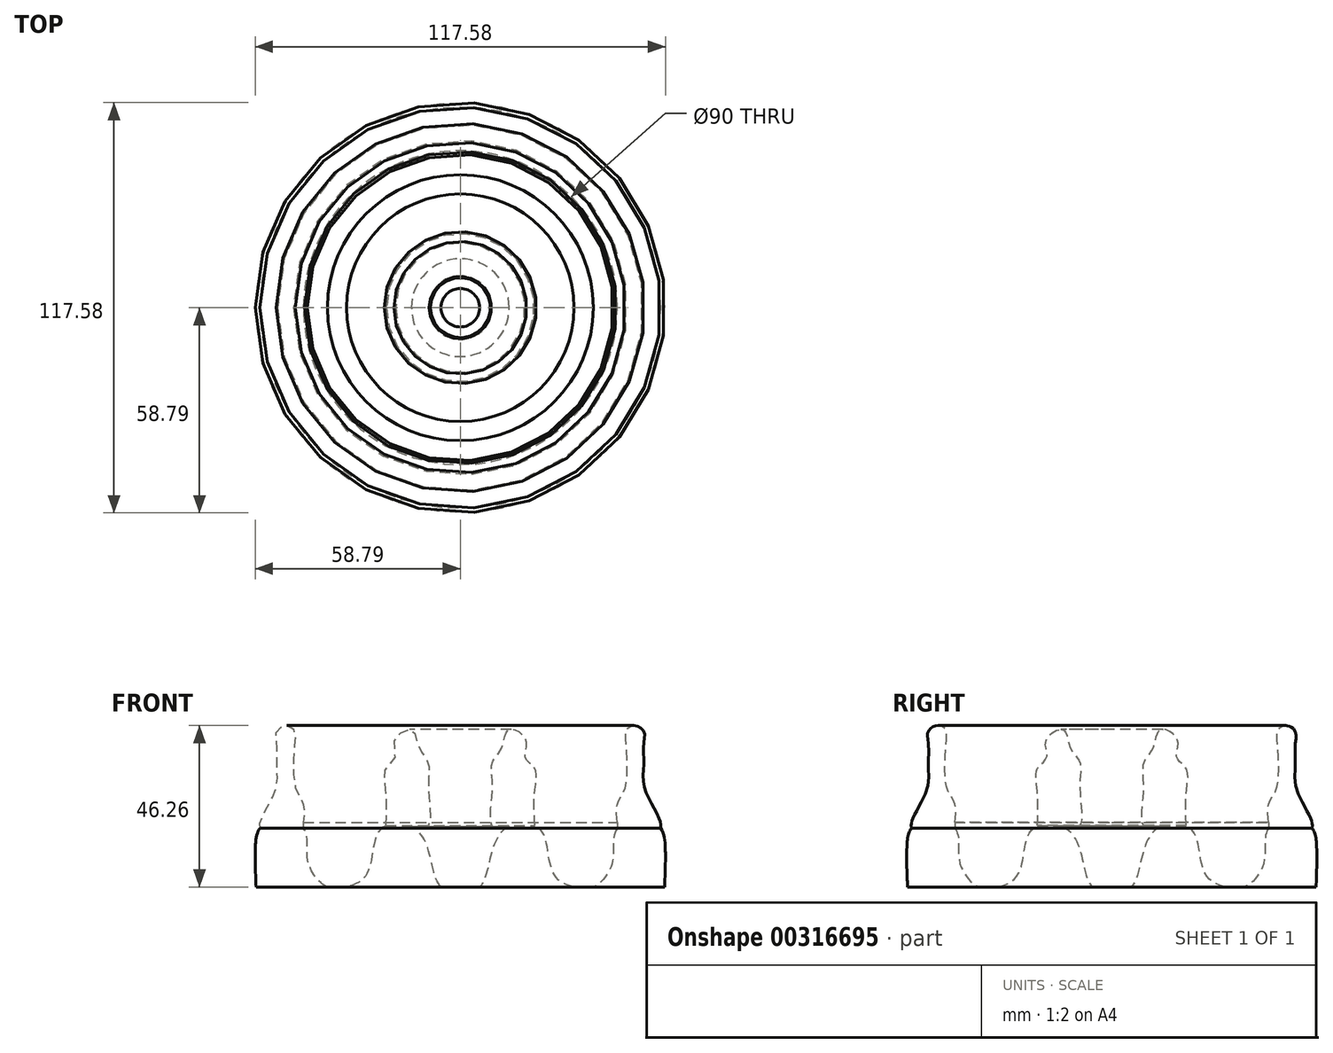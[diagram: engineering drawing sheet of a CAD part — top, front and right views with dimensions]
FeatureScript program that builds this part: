
annotation { "Feature Type Name" : "Feature", "Feature Type Description" : "" }
export const myFeature = defineFeature(function(context is Context, id is Id, definition is map)
    precondition{}
    {
        {
            var Q0;
            Q0=qCreatedBy(makeId("Front.planeOp"),FACE);
            var sketch = newSketch(context, id + "F0", { "sketchPlane" : qUnion([Q0])});
            skLineSegment(sketch, "E0", {"start": v(0, 0) * mm, "end": v(0, 76.57) * mm});
            skFitSpline(sketch, "E1", {"points": [v(0, 0) * mm, v(-5.51, 0) * mm, v(-9.18, 10.68) * mm, v(-14, 17.33) * mm, v(-21.35, 17.56) * mm, v(-24.34, 13.89) * mm, v(-25.71, 6.77) * mm, v(-28, 2.18) * mm, v(-32.6, 0) * mm, v(-38.11, 0) * mm, v(-42.01, 3.56) * mm, v(-43.85, 8.84) * mm, v(-45, 16.87) * mm, v(-52.57, 18.48) * mm, v(-57.4, 16.87) * mm, v(-58.77, 10.45) * mm, v(-58.54, 0) * mm], "startDerivative": vector(-109.33, -30.5) * mm, "endDerivative": vector(5.88, -136.92) * mm});
            skFitSpline(sketch, "E2", {"points": [v(-57.4, 16.87) * mm, v(-57.4, 18.48) * mm, v(-55.1, 23.3) * mm, v(-52.57, 29.5) * mm, v(-52.57, 35.24) * mm, v(-52.57, 40.98) * mm, v(-52.57, 44.65) * mm, v(-49.82, 46.26) * mm, v(-47.75, 45.11) * mm, v(-47.52, 40.52) * mm, v(-47.3, 28.58) * mm, v(-45, 23.76) * mm, v(-45, 18.48) * mm], "startDerivative": vector(-4.72, 29.71) * mm, "endDerivative": vector(-8.21, -64.78) * mm});
            skFitSpline(sketch, "E3", {"points": [v(-21.35, 17.56) * mm, v(-21.35, 27.66) * mm, v(-21.35, 33.86) * mm, v(-18.6, 37.3) * mm, v(-18.83, 42.13) * mm, v(-14, 45.11) * mm, v(-11.94, 40.06) * mm, v(-9.18, 35.7) * mm, v(-9.18, 28.35) * mm, v(-9.18, 17.33) * mm, v(-14, 17.33) * mm], "startDerivative": vector(4.02, 83.06) * mm, "endDerivative": vector(-68.03, 18.74) * mm});
            skFitSpline(sketch, "E4", {"points": [v(-58.54, 0) * mm, v(0, 0) * mm], "startDerivative": vector(58.54, 0) * mm, "endDerivative": vector(58.54, 0) * mm});
            skFitSpline(sketch, "E5", {"points": [v(-45, 18.48) * mm, v(-45, 16.87) * mm], "startDerivative": vector(0, -1.6) * mm, "endDerivative": vector(0, -1.6) * mm});
            skSolve(sketch);
        }
        {
            var Q0;
            {var subQ0=sQuery(id+"F0.wireOp",EDGE,"E1");var subQ1=makeQuery(id+"F0.imprint","INTERSECT",VERTEX,{"derivedFrom":[subQ0,sQuery(id+"F0.wireOp",EDGE,"E5")]});Q0=makeQuery(id+"F0.imprint","IMPRINT",FACE,{"disambiguationData":[TD([[makeQuery(id+"F0.imprint","IMPRINT",EDGE,{"disambiguationData":[TD([[subQ1,1.0]])],"derivedFrom":subQ0}),1.0]])]});}
            var Q1;
            {var subQ0=sQuery(id+"F0.wireOp",EDGE,"E2");Q1=makeQuery(id+"F0.imprint","IMPRINT",FACE,{"disambiguationData":[TD([[makeQuery(id+"F0.imprint","IMPRINT",EDGE,{"derivedFrom":subQ0}),-1.0]])]});}
            var Q2;
            {var subQ0=sQuery(id+"F0.wireOp",EDGE,"E3");var subQ1=sQuery(id+"F0.wireOp",EDGE,"E1");var subQ2=makeQuery(id+"F0.imprint","INTERSECT",VERTEX,{"disambiguationData":[OD(1.0)],"derivedFrom":[subQ1,subQ0]});Q2=makeQuery(id+"F0.imprint","IMPRINT",FACE,{"disambiguationData":[TD([[makeQuery(id+"F0.imprint","IMPRINT",EDGE,{"disambiguationData":[TD([[subQ2,1.0]])],"derivedFrom":subQ1}),1.0]])]});}
            var Q3;
            {var subQ0=sQuery(id+"F0.wireOp",EDGE,"E3");Q3=makeQuery(id+"F0.imprint","IMPRINT",FACE,{"disambiguationData":[TD([[makeQuery(id+"F0.imprint","IMPRINT",EDGE,{"derivedFrom":subQ0}),-1.0]])]});}
            var Q4;
            {var subQ0=sQuery(id+"F0.wireOp",EDGE,"E4");var subQ1=sQuery(id+"F0.wireOp",EDGE,"E1");var subQ2=makeQuery(id+"F0.imprint","INTERSECT",VERTEX,{"disambiguationData":[OD(3.0)],"derivedFrom":[subQ1,subQ0]});Q4=makeQuery(id+"F0.imprint","IMPRINT",FACE,{"disambiguationData":[TD([[makeQuery(id+"F0.imprint","IMPRINT",EDGE,{"disambiguationData":[TD([[subQ2,-1.0]])],"derivedFrom":subQ1}),-1.0]])]});}
            var Q5;
            Q5=sQuery(id+"F0.wireOp",EDGE,"E0");
            revolve(context, id + "F1", {"entities" : qUnion([Q0, Q1, Q2, Q3, Q4]), "axis" : qUnion([Q5]), "revolveType" : RevolveType.FULL});
        }
    });
